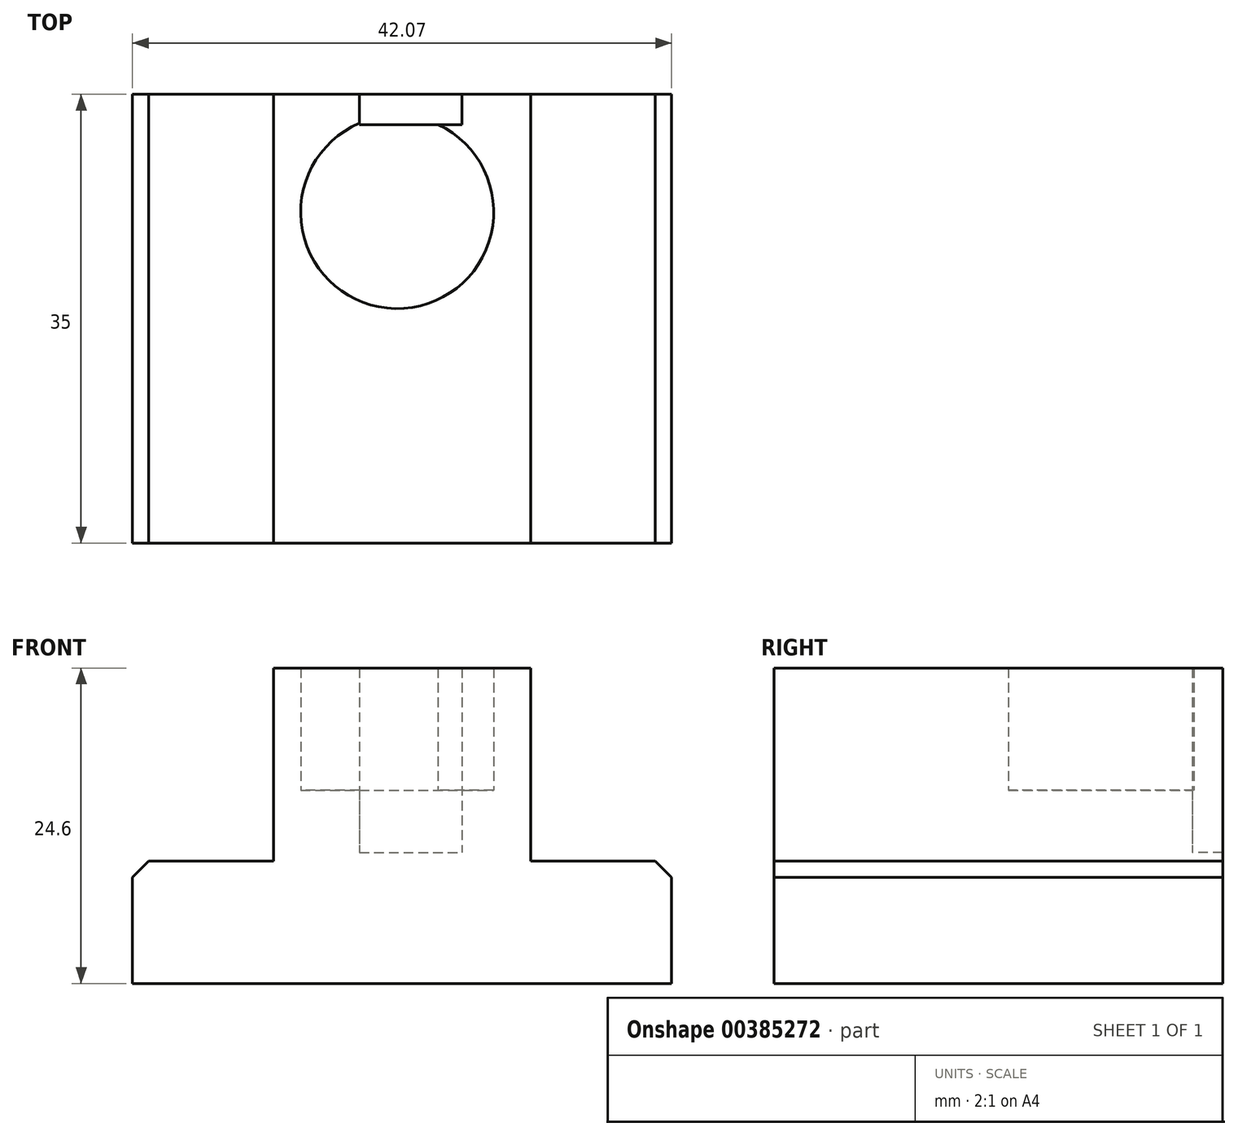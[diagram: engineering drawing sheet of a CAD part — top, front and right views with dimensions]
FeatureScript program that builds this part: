
annotation { "Feature Type Name" : "Feature", "Feature Type Description" : "" }
export const myFeature = defineFeature(function(context is Context, id is Id, definition is map)
    precondition{}
    {
        {
            var Q0;
            Q0=qCreatedBy(makeId("Front.planeOp"),FACE);
            var sketch = newSketch(context, id + "F0", { "sketchPlane" : qUnion([Q0])});
            skLineSegment(sketch, "E0", {"start": v(-22.02, 0) * mm, "end": v(19.86, 0) * mm});
            skLineSegment(sketch, "E1", {"start": v(19.86, 0) * mm, "end": v(19.86, 9.53) * mm});
            skLineSegment(sketch, "E2", {"start": v(19.86, 9.53) * mm, "end": v(8.86, 9.53) * mm});
            skLineSegment(sketch, "E3", {"start": v(-22.2, 9.53) * mm, "end": v(-22.2, 0) * mm});
            skLineSegment(sketch, "E4", {"start": v(-22.02, 0) * mm, "end": v(-22.2, 0) * mm});
            skLineSegment(sketch, "E5", {"start": v(8.86, 9.53) * mm, "end": v(8.86, 24.6) * mm});
            skLineSegment(sketch, "E6", {"start": v(8.86, 24.6) * mm, "end": v(-11.21, 24.6) * mm});
            skLineSegment(sketch, "E7", {"start": v(-11.21, 24.6) * mm, "end": v(-11.21, 9.53) * mm});
            skLineSegment(sketch, "E8.trimOffspring", {"start": v(-11.21, 9.53) * mm, "end": v(-22.2, 9.53) * mm});
            skSolve(sketch);
        }
        {
            var Q0;
            Q0=makeQuery(id+"F0.imprint","IMPRINT",FACE,{"disambiguationData":[TD([[makeQuery(id+"F0.imprint","IMPRINT",EDGE,{"derivedFrom":sQuery(id+"F0.wireOp",EDGE,"E0")}),1.0]])]});
            var Q1;
            {var subQ0=sQuery(id+"F0.wireOp",EDGE,"svC2swnz-MnSQ-uOyC-Sphh-vKwHXSaeiggU");Q1=makeQuery(id+"F0.imprint","IMPRINT",FACE,{"disambiguationData":[TD([[makeQuery(id+"F0.imprint","IMPRINT",EDGE,{"derivedFrom":subQ0}),1.0]])]});}
            extrude(context, id + "F1", {"entities" : qUnion([Q0, Q1]), "depth" : 35 * mm});
        }
        {
            var Q0;
            Q0=qCreatedBy(makeId("Top.planeOp"),FACE);
            var sketch = newSketch(context, id + "F2", { "sketchPlane" : qUnion([Q0])});
            skCircle(sketch, "E9", {"center": v(-1.56, -9.18) * mm, "radius": 7.53 * mm});
            skSolve(sketch);
        }
        {
            var Q0;
            Q0=makeQuery(id+"F2.imprint","IMPRINT",FACE,{"disambiguationData":[TD([[makeQuery(id+"F2.imprint","IMPRINT",EDGE,{"derivedFrom":sQuery(id+"F2.wireOp",EDGE,"E9")}),1.0]])]});
            extrude(context, id + "F3", {"entities" : qUnion([Q0]), "operationType" : NewBodyOperationType.REMOVE, "depth" : 24.64 * mm});
        }
        {
            var Q0;
            Q0=makeQuery(id+"F2.imprint","IMPRINT",FACE,{"disambiguationData":[TD([[makeQuery(id+"F2.imprint","IMPRINT",EDGE,{"derivedFrom":sQuery(id+"F2.wireOp",EDGE,"E9")}),1.0]])]});
            extrude(context, id + "F4", {"entities" : qUnion([Q0]), "operationType" : NewBodyOperationType.ADD, "depth" : 15.06 * mm});
        }
        {
            var Q0;
            Q0=makeQuery(id+"F0.imprint","IMPRINT",FACE,{"disambiguationData":[TD([[makeQuery(id+"F0.imprint","IMPRINT",EDGE,{"derivedFrom":sQuery(id+"F0.wireOp",EDGE,"E0")}),1.0]])]});
            var sketch = newSketch(context, id + "F5", { "sketchPlane" : qUnion([Q0])});
            skLineSegment(sketch, "E10.bottom", {"start": v(-4.5, 24.6) * mm, "end": v(3.5, 24.6) * mm});
            skLineSegment(sketch, "E10.top", {"start": v(-4.5, 10.23) * mm, "end": v(3.5, 10.23) * mm});
            skLineSegment(sketch, "E10.left", {"start": v(-4.5, 24.6) * mm, "end": v(-4.5, 10.23) * mm});
            skLineSegment(sketch, "E10.right", {"start": v(3.5, 24.6) * mm, "end": v(3.5, 10.23) * mm});
            skPoint(sketch, "E10.middle", {"position": v(-0.5, 17.41) * mm});
            skSolve(sketch);
        }
        {
            var Q0;
            {var subQ0=sQuery(id+"F5.wireOp",EDGE,"E10.top");Q0=makeQuery(id+"F5.imprint","IMPRINT",FACE,{"disambiguationData":[TD([[makeQuery(id+"F5.imprint","IMPRINT",EDGE,{"derivedFrom":subQ0}),1.0]])]});}
            extrude(context, id + "F6", {"entities" : qUnion([Q0]), "operationType" : NewBodyOperationType.REMOVE, "endBound" : BoundingType.SYMMETRIC, "oppositeDirection" : true, "depth" : 4.72 * mm});
        }
        {
            var Q0;
            Q0=makeQuery(id+"F1.opExtrude","SWEPT_EDGE",EDGE,{"disambiguationData":[OSD([sQuery(id+"F0.wireOp",EDGE,"E1"),sQuery(id+"F0.wireOp",EDGE,"E2")])]});
            var Q1;
            Q1=makeQuery(id+"F1.opExtrude","SWEPT_EDGE",EDGE,{"disambiguationData":[OSD([sQuery(id+"F0.wireOp",EDGE,"E3"),sQuery(id+"F0.wireOp",EDGE,"E8.trimOffspring")])]});
            chamfer(context, id + "F7", {"entities" : qUnion([Q0, Q1]), "width" : 1.27 * mm, "tangentPropagation" : true});
        }
    });
